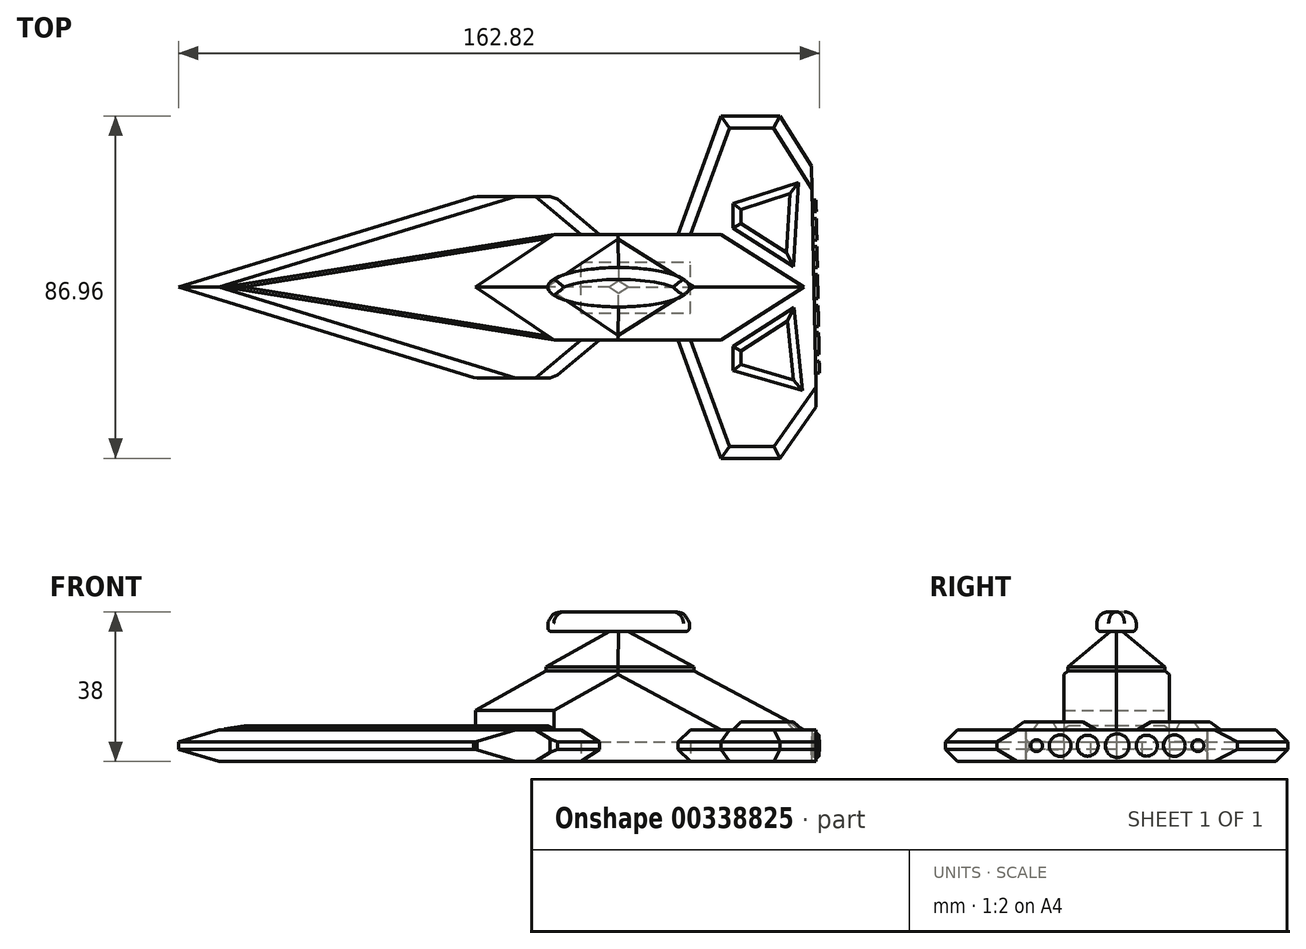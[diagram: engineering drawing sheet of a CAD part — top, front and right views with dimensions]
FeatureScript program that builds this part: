
annotation { "Feature Type Name" : "Feature", "Feature Type Description" : "" }
export const myFeature = defineFeature(function(context is Context, id is Id, definition is map)
    precondition{}
    {
        {
            var Q0;
            Q0=qCreatedBy(makeId("Top.planeOp"),FACE);
            var sketch = newSketch(context, id + "F0", { "sketchPlane" : qUnion([Q0])});
            skLineSegment(sketch, "E0", {"start": v(0, 0) * mm, "end": v(75, 0) * mm});
            skLineSegment(sketch, "E1", {"start": v(0, 0) * mm, "end": v(75.4, 23.05) * mm});
            skLineSegment(sketch, "E2", {"start": v(0, 0) * mm, "end": v(75.4, -23.05) * mm});
            skLineSegment(sketch, "E3", {"start": v(75.4, 23.05) * mm, "end": v(75.4, -23.05) * mm});
            skLineSegment(sketch, "E4", {"start": v(75.4, 23.05) * mm, "end": v(95.4, 23.05) * mm});
            skLineSegment(sketch, "E5", {"start": v(75.4, -23.05) * mm, "end": v(95.4, -23.05) * mm});
            skLineSegment(sketch, "E6", {"start": v(95.4, -23.05) * mm, "end": v(95.4, 23.05) * mm});
            skLineSegment(sketch, "E7", {"start": v(95.4, 23.05) * mm, "end": v(106.9, 13.41) * mm});
            skLineSegment(sketch, "E8", {"start": v(95.4, -23.05) * mm, "end": v(106.9, -13.41) * mm});
            skLineSegment(sketch, "E9", {"start": v(106.9, 13.41) * mm, "end": v(106.9, -13.41) * mm});
            skLineSegment(sketch, "E10", {"start": v(106.9, 13.41) * mm, "end": v(126.9, 13.41) * mm});
            skLineSegment(sketch, "E11", {"start": v(106.9, -13.41) * mm, "end": v(126.9, -13.41) * mm});
            skLineSegment(sketch, "E12", {"start": v(126.9, 13.41) * mm, "end": v(126.9, -13.41) * mm});
            skLineSegment(sketch, "E13", {"start": v(126.9, 13.41) * mm, "end": v(137.84, 43.48) * mm});
            skLineSegment(sketch, "E14", {"start": v(126.9, -13.41) * mm, "end": v(137.84, -43.48) * mm});
            skLineSegment(sketch, "E15", {"start": v(137.84, 43.48) * mm, "end": v(152.84, 43.48) * mm});
            skLineSegment(sketch, "E16", {"start": v(137.84, -43.48) * mm, "end": v(152.84, -43.48) * mm});
            skLineSegment(sketch, "E17", {"start": v(152.84, 43.48) * mm, "end": v(152.84, -43.48) * mm});
            skLineSegment(sketch, "E18", {"start": v(152.84, 43.48) * mm, "end": v(160.79, 30.76) * mm});
            skLineSegment(sketch, "E19", {"start": v(152.84, -43.48) * mm, "end": v(161.98, -30.42) * mm});
            skLineSegment(sketch, "E20", {"start": v(160.79, 30.76) * mm, "end": v(161.98, -30.42) * mm});
            skSolve(sketch);
        }
        {
            var Q0;
            Q0 = qSketchRegion(id + "F0", true);
            extrude(context, id + "F1", {"entities" : qUnion([Q0]), "depth" : 8 * mm});
        }
        {
            var Q0;
            Q0=makeQuery(id+"F1.opExtrude","SWEPT_FACE",FACE,{"disambiguationData":[OSD([sQuery(id+"F0.wireOp",EDGE,"E20")])]});
            var sketch = newSketch(context, id + "F2", { "sketchPlane" : qUnion([Q0])});
            skCircle(sketch, "E21", {"center": v(-2.98, 4) * mm, "radius": 3 * mm});
            skPoint(sketch, "E21.centerSnap0", {"position": v(-33.58, 4) * mm});
            skPoint(sketch, "E21.centerSnap1", {"position": v(-2.98, 0) * mm});
            skCircle(sketch, "E22", {"center": v(-10.48, 4) * mm, "radius": 2.66 * mm});
            skCircle(sketch, "E23", {"center": v(4.52, 4) * mm, "radius": 2.66 * mm});
            skCircle(sketch, "E24", {"center": v(-23.48, 4) * mm, "radius": 1.5 * mm});
            skCircle(sketch, "E25", {"center": v(17.52, 4) * mm, "radius": 1.5 * mm});
            skCircle(sketch, "E26", {"center": v(11.52, 4) * mm, "radius": 2.75 * mm});
            skCircle(sketch, "E27", {"center": v(-17.48, 4) * mm, "radius": 2.75 * mm});
            skSolve(sketch);
        }
        {
            var Q0;
            Q0 = qSketchRegion(id + "F2", true);
            extrude(context, id + "F3", {"entities" : qUnion([Q0]), "operationType" : NewBodyOperationType.ADD, "depth" : 1 * mm});
        }
        {
            var Q0;
            Q0=makeQuery(id+"F1.opExtrude","CAP_FACE",FACE,{"disambiguationData":[OSD([sQuery(id+"F0.wireOp",EDGE,"E1"),sQuery(id+"F0.wireOp",EDGE,"E2"),sQuery(id+"F0.wireOp",EDGE,"E4"),sQuery(id+"F0.wireOp",EDGE,"E5"),sQuery(id+"F0.wireOp",EDGE,"E7"),sQuery(id+"F0.wireOp",EDGE,"E8"),sQuery(id+"F0.wireOp",EDGE,"E10"),sQuery(id+"F0.wireOp",EDGE,"E11"),sQuery(id+"F0.wireOp",EDGE,"E13"),sQuery(id+"F0.wireOp",EDGE,"E14"),sQuery(id+"F0.wireOp",EDGE,"E15"),sQuery(id+"F0.wireOp",EDGE,"E16"),sQuery(id+"F0.wireOp",EDGE,"E18"),sQuery(id+"F0.wireOp",EDGE,"E19"),sQuery(id+"F0.wireOp",EDGE,"E20")])],"isStart":false});
            var sketch = newSketch(context, id + "F4", { "sketchPlane" : qUnion([Q0])});
            skLineSegment(sketch, "E28", {"start": v(95.4, 13.41) * mm, "end": v(75.4, 0) * mm});
            skLineSegment(sketch, "E29", {"start": v(75.4, 0) * mm, "end": v(95.4, -13.41) * mm});
            skLineSegment(sketch, "E30", {"start": v(95.4, -13.41) * mm, "end": v(137.84, -13.41) * mm});
            skLineSegment(sketch, "E31", {"start": v(137.84, -13.41) * mm, "end": v(137.84, 13.41) * mm});
            skLineSegment(sketch, "E32", {"start": v(137.84, 13.41) * mm, "end": v(95.4, 13.41) * mm});
            skLineSegment(sketch, "E33", {"start": v(137.84, 13.41) * mm, "end": v(158.9, 0) * mm});
            skLineSegment(sketch, "E34", {"start": v(158.9, 0) * mm, "end": v(137.84, -13.41) * mm});
            skSolve(sketch);
        }
        {
            var Q0;
            Q0=makeQuery(id+"F4.imprint","IMPRINT",FACE,{"disambiguationData":[TD([[makeQuery(id+"F4.imprint","IMPRINT",EDGE,{"derivedFrom":sQuery(id+"F4.wireOp",EDGE,"E31")}),-1.0]])]});
            var Q1;
            {var subQ4=sQuery(id+"F4.wireOp",EDGE,"E28");Q1=makeQuery(id+"F4.imprint","IMPRINT",FACE,{"disambiguationData":[TD([[makeQuery(id+"F4.imprint","IMPRINT",EDGE,{"derivedFrom":subQ4}),1.0]])]});}
            extrude(context, id + "F5", {"entities" : qUnion([Q0, Q1]), "operationType" : NewBodyOperationType.ADD, "depth" : 15 * mm});
        }
        {
            var Q0;
            Q0=makeQuery(id+"F5.opExtrude","CAP_EDGE",EDGE,{"disambiguationData":[OSD([sQuery(id+"F4.wireOp",EDGE,"E29")])],"isStart":false});
            var Q1;
            Q1=makeQuery(id+"F5.opExtrude","CAP_EDGE",EDGE,{"disambiguationData":[OSD([sQuery(id+"F4.wireOp",EDGE,"E28")])],"isStart":false});
            chamfer(context, id + "F6", {"entities" : qUnion([Q0, Q1]), "width" : 10 * mm, "tangentPropagation" : true});
        }
        {
            var Q0;
            Q0=makeQuery(id+"F5.opExtrude","CAP_EDGE",EDGE,{"disambiguationData":[OSD([sQuery(id+"F4.wireOp",EDGE,"E33")])],"isStart":false});
            var Q1;
            Q1=makeQuery(id+"F5.opExtrude","CAP_EDGE",EDGE,{"disambiguationData":[OSD([sQuery(id+"F4.wireOp",EDGE,"E34")])],"isStart":false});
            chamfer(context, id + "F7", {"entities" : qUnion([Q0, Q1]), "width" : 15 * mm, "tangentPropagation" : true});
        }
        {
            var Q0;
            Q0=makeQuery(id+"F5.opExtrude","CAP_FACE",FACE,{"disambiguationData":[OSD([sQuery(id+"F4.wireOp",EDGE,"E28"),sQuery(id+"F4.wireOp",EDGE,"E29"),sQuery(id+"F4.wireOp",EDGE,"E30"),sQuery(id+"F4.wireOp",EDGE,"E32"),sQuery(id+"F4.wireOp",EDGE,"E33"),sQuery(id+"F4.wireOp",EDGE,"E34")])],"isStart":false});
            var sketch = newSketch(context, id + "F8", { "sketchPlane" : qUnion([Q0])});
            skLineSegment(sketch, "E35", {"start": v(111.68, 12.28) * mm, "end": v(111.68, 0) * mm});
            skLineSegment(sketch, "E36", {"start": v(111.68, 0) * mm, "end": v(111.68, -12.28) * mm});
            skLineSegment(sketch, "E37", {"start": v(111.68, -12.28) * mm, "end": v(130.98, 0) * mm});
            skLineSegment(sketch, "E38", {"start": v(130.98, 0) * mm, "end": v(111.68, 0) * mm});
            skLineSegment(sketch, "E39", {"start": v(93.36, 0) * mm, "end": v(111.68, 0) * mm});
            skLineSegment(sketch, "E40", {"start": v(111.68, 12.28) * mm, "end": v(93.36, 0) * mm});
            skLineSegment(sketch, "E41", {"start": v(130.98, 0) * mm, "end": v(111.68, 12.28) * mm});
            skSolve(sketch);
        }
        {
            var Q0;
            Q0=makeQuery(id+"F8.imprint","IMPRINT",FACE,{"disambiguationData":[TD([[makeQuery(id+"F8.imprint","IMPRINT",EDGE,{"derivedFrom":sQuery(id+"F8.wireOp",EDGE,"E36")}),-1.0]])]});
            var Q1;
            Q1=makeQuery(id+"F8.imprint","IMPRINT",FACE,{"disambiguationData":[TD([[makeQuery(id+"F8.imprint","IMPRINT",EDGE,{"derivedFrom":sQuery(id+"F8.wireOp",EDGE,"E36")}),1.0]])]});
            var Q2;
            Q2=makeQuery(id+"F8.imprint","IMPRINT",FACE,{"disambiguationData":[TD([[makeQuery(id+"F8.imprint","IMPRINT",EDGE,{"derivedFrom":sQuery(id+"F8.wireOp",EDGE,"E35")}),-1.0]])]});
            var Q3;
            Q3=makeQuery(id+"F8.imprint","IMPRINT",FACE,{"disambiguationData":[TD([[makeQuery(id+"F8.imprint","IMPRINT",EDGE,{"derivedFrom":sQuery(id+"F8.wireOp",EDGE,"E35")}),1.0]])]});
            extrude(context, id + "F9", {"entities" : qUnion([Q0, Q1, Q2, Q3]), "operationType" : NewBodyOperationType.ADD, "depth" : 10 * mm});
        }
        {
            var Q0;
            Q0=makeQuery(id+"F9.opExtrude","CAP_EDGE",EDGE,{"disambiguationData":[OSD([sQuery(id+"F8.wireOp",EDGE,"E37")])],"isStart":false});
            var Q1;
            Q1=makeQuery(id+"F9.opExtrude","CAP_EDGE",EDGE,{"disambiguationData":[OSD([sQuery(id+"F4.wireOp",EDGE,"E28"),sQuery(id+"F4.wireOp",EDGE,"E29"),sQuery(id+"F4.wireOp",EDGE,"E30"),sQuery(id+"F4.wireOp",EDGE,"E32"),sQuery(id+"F4.wireOp",EDGE,"E33"),sQuery(id+"F4.wireOp",EDGE,"E34")])],"isStart":false});
            var Q2;
            Q2=makeQuery(id+"F9.opExtrude","CAP_EDGE",EDGE,{"disambiguationData":[OSD([sQuery(id+"F8.wireOp",EDGE,"E40")])],"isStart":false});
            var Q3;
            Q3=makeQuery(id+"F9.opExtrude","CAP_EDGE",EDGE,{"disambiguationData":[OSD([sQuery(id+"F8.wireOp",EDGE,"E41")])],"isStart":false});
            chamfer(context, id + "F10", {"entities" : qUnion([Q0, Q1, Q2, Q3]), "width" : 9 * mm, "tangentPropagation" : true});
        }
        {
            var Q0;
            Q0=makeQuery(id+"F9.opExtrude","CAP_FACE",FACE,{"disambiguationData":[OSD([sQuery(id+"F4.wireOp",EDGE,"E28"),sQuery(id+"F4.wireOp",EDGE,"E29"),sQuery(id+"F4.wireOp",EDGE,"E30"),sQuery(id+"F4.wireOp",EDGE,"E32"),sQuery(id+"F4.wireOp",EDGE,"E33"),sQuery(id+"F4.wireOp",EDGE,"E34"),sQuery(id+"F8.wireOp",EDGE,"E37"),sQuery(id+"F8.wireOp",EDGE,"E40"),sQuery(id+"F8.wireOp",EDGE,"E41")])],"isStart":false});
            var sketch = newSketch(context, id + "F11", { "sketchPlane" : qUnion([Q0])});
            skEllipse(sketch, "E42", {"center": v(111.8, 0) * mm, "majorRadius": 18 * mm, "minorRadius": 5 * mm, "majorAxis": v(-1, 0)});
            skSolve(sketch);
        }
        {
            var Q0;
            Q0 = qSketchRegion(id + "F11", true);
            extrude(context, id + "F12", {"entities" : qUnion([Q0]), "operationType" : NewBodyOperationType.ADD, "depth" : 5 * mm});
        }
        {
            var Q0;
            Q0=makeQuery(id+"F12.opExtrude","CAP_EDGE",EDGE,{"disambiguationData":[OSD([sQuery(id+"F11.wireOp",EDGE,"E42")])],"isStart":false});
            fillet(context, id + "F13", {"entities" : qUnion([Q0]), "radius" : 3 * mm, "tangentPropagation" : true, "allowEdgeOverflow" : false});
        }
        {
            var Q0;
            Q0=makeQuery(id+"F12.opExtrude","CAP_EDGE",EDGE,{"disambiguationData":[OSD([sQuery(id+"F11.wireOp",EDGE,"E42")])],"isStart":true});
            fillet(context, id + "F14", {"entities" : qUnion([Q0]), "radius" : 1 * mm, "tangentPropagation" : true, "allowEdgeOverflow" : false});
        }
        {
            var Q0;
            {var subQ0=sQuery(id+"F0.wireOp",EDGE,"E11");var subQ1=sQuery(id+"F0.wireOp",EDGE,"E10");var subQ2=sQuery(id+"F0.wireOp",EDGE,"E8");var subQ3=sQuery(id+"F0.wireOp",EDGE,"E7");var subQ4=sQuery(id+"F0.wireOp",EDGE,"E1");var subQ5=sQuery(id+"F0.wireOp",EDGE,"E5");var subQ6=sQuery(id+"F0.wireOp",EDGE,"E2");var subQ7=sQuery(id+"F0.wireOp",EDGE,"E4");Q0=makeQuery(id+"F5.boolean.opBoolean","SPLIT",FACE,{"disambiguationData":[TD([makeQuery(id+"F1.opExtrude","SWEPT_FACE",FACE,{"disambiguationData":[OSD([subQ4])]})])],"derivedFrom":makeQuery(id+"F1.opExtrude","CAP_FACE",FACE,{"disambiguationData":[OSD([subQ4,subQ6,subQ7,subQ5,subQ3,subQ2,subQ1,subQ0,sQuery(id+"F0.wireOp",EDGE,"E13"),sQuery(id+"F0.wireOp",EDGE,"E14"),sQuery(id+"F0.wireOp",EDGE,"E15"),sQuery(id+"F0.wireOp",EDGE,"E16"),sQuery(id+"F0.wireOp",EDGE,"E18"),sQuery(id+"F0.wireOp",EDGE,"E19"),sQuery(id+"F0.wireOp",EDGE,"E20")])],"isStart":false})});}
            var sketch = newSketch(context, id + "F15", { "sketchPlane" : qUnion([Q0])});
            skLineSegment(sketch, "E43", {"start": v(11.59, 0) * mm, "end": v(95.4, 13.41) * mm});
            skLineSegment(sketch, "E44", {"start": v(95.4, 13.41) * mm, "end": v(75.4, 0) * mm});
            skLineSegment(sketch, "E45", {"start": v(75.4, 0) * mm, "end": v(95.4, -13.41) * mm});
            skLineSegment(sketch, "E46", {"start": v(95.4, -13.41) * mm, "end": v(11.59, 0) * mm});
            skLineSegment(sketch, "E47", {"start": v(75.4, 0) * mm, "end": v(11.59, 0) * mm});
            skSolve(sketch);
        }
        {
            var Q0;
            Q0=makeQuery(id+"F15.imprint","IMPRINT",FACE,{"disambiguationData":[TD([[makeQuery(id+"F15.imprint","IMPRINT",EDGE,{"derivedFrom":sQuery(id+"F15.wireOp",EDGE,"E43")}),-1.0]])]});
            var Q1;
            Q1=makeQuery(id+"F15.imprint","IMPRINT",FACE,{"disambiguationData":[TD([[makeQuery(id+"F15.imprint","IMPRINT",EDGE,{"derivedFrom":sQuery(id+"F15.wireOp",EDGE,"E45")}),-1.0]])]});
            extrude(context, id + "F16", {"entities" : qUnion([Q0, Q1]), "operationType" : NewBodyOperationType.ADD, "depth" : 1 * mm});
        }
        {
            var Q0;
            Q0=makeQuery(id+"F16.opExtrude","CAP_EDGE",EDGE,{"disambiguationData":[OSD([sQuery(id+"F15.wireOp",EDGE,"E46")])],"isStart":false});
            var Q1;
            Q1=makeQuery(id+"F16.opExtrude","CAP_EDGE",EDGE,{"disambiguationData":[OSD([sQuery(id+"F15.wireOp",EDGE,"E43")])],"isStart":false});
            chamfer(context, id + "F17", {"entities" : qUnion([Q0, Q1]), "width" : 0.8 * mm, "tangentPropagation" : true});
        }
        {
            var Q0;
            {var subQ0=sQuery(id+"F0.wireOp",EDGE,"E20");var subQ1=sQuery(id+"F0.wireOp",EDGE,"E19");var subQ2=sQuery(id+"F0.wireOp",EDGE,"E18");var subQ3=sQuery(id+"F0.wireOp",EDGE,"E16");var subQ4=sQuery(id+"F0.wireOp",EDGE,"E15");var subQ5=sQuery(id+"F0.wireOp",EDGE,"E10");var subQ6=sQuery(id+"F0.wireOp",EDGE,"E11");var subQ7=sQuery(id+"F0.wireOp",EDGE,"E13");var subQ8=sQuery(id+"F0.wireOp",EDGE,"E14");Q0=makeQuery(id+"F5.boolean.opBoolean","SPLIT",FACE,{"disambiguationData":[TD([makeQuery(id+"F1.opExtrude","SWEPT_FACE",FACE,{"disambiguationData":[OSD([subQ7])]})])],"derivedFrom":makeQuery(id+"F1.opExtrude","CAP_FACE",FACE,{"disambiguationData":[OSD([sQuery(id+"F0.wireOp",EDGE,"E1"),sQuery(id+"F0.wireOp",EDGE,"E2"),sQuery(id+"F0.wireOp",EDGE,"E4"),sQuery(id+"F0.wireOp",EDGE,"E5"),sQuery(id+"F0.wireOp",EDGE,"E7"),sQuery(id+"F0.wireOp",EDGE,"E8"),subQ5,subQ6,subQ7,subQ8,subQ4,subQ3,subQ2,subQ1,subQ0])],"isStart":false})});}
            var sketch = newSketch(context, id + "F18", { "sketchPlane" : qUnion([Q0])});
            skLineSegment(sketch, "E48", {"start": v(137.84, 13.41) * mm, "end": v(137.84, 23.41) * mm});
            skLineSegment(sketch, "E49", {"start": v(137.84, 23.41) * mm, "end": v(160.79, 30.76) * mm});
            skLineSegment(sketch, "E50", {"start": v(160.79, 30.76) * mm, "end": v(158.9, 0) * mm});
            skLineSegment(sketch, "E51", {"start": v(137.84, -13.41) * mm, "end": v(137.84, -23.41) * mm});
            skLineSegment(sketch, "E52", {"start": v(137.84, -23.41) * mm, "end": v(161.98, -30.42) * mm});
            skLineSegment(sketch, "E53", {"start": v(161.98, -30.42) * mm, "end": v(158.9, 0) * mm});
            skSolve(sketch);
        }
        {
            var Q0;
            Q0=makeQuery(id+"F18.imprint","IMPRINT",FACE,{"disambiguationData":[TD([[makeQuery(id+"F18.imprint","IMPRINT",EDGE,{"derivedFrom":sQuery(id+"F18.wireOp",EDGE,"E48")}),-1.0]])]});
            var Q1;
            Q1=makeQuery(id+"F18.imprint","IMPRINT",FACE,{"disambiguationData":[TD([[makeQuery(id+"F18.imprint","IMPRINT",EDGE,{"derivedFrom":sQuery(id+"F18.wireOp",EDGE,"E51")}),1.0]])]});
            extrude(context, id + "F19", {"entities" : qUnion([Q0, Q1]), "depth" : 2 * mm});
        }
        {
            var Q0;
            Q0=makeQuery(id+"F19.opExtrude","CAP_EDGE",EDGE,{"disambiguationData":[OSD([sQuery(id+"F18.wireOp",EDGE,"E51")])],"isStart":false});
            var Q1;
            Q1=makeQuery(id+"F19.opExtrude","CAP_EDGE",EDGE,{"disambiguationData":[OSD([sQuery(id+"F18.wireOp",EDGE,"E52")])],"isStart":false});
            var Q2;
            Q2=makeQuery(id+"F19.opExtrude","CAP_EDGE",EDGE,{"disambiguationData":[OSD([sQuery(id+"F18.wireOp",EDGE,"E48")])],"isStart":false});
            var Q3;
            Q3=makeQuery(id+"F19.opExtrude","CAP_EDGE",EDGE,{"disambiguationData":[OSD([sQuery(id+"F18.wireOp",EDGE,"E49")])],"isStart":false});
            var Q4;
            Q4=makeQuery(id+"F19.opExtrude","CAP_EDGE",EDGE,{"disambiguationData":[OSD([sQuery(id+"F18.wireOp",EDGE,"E50")])],"isStart":false});
            var Q5;
            Q5=makeQuery(id+"F19.opExtrude","CAP_EDGE",EDGE,{"disambiguationData":[OSD([sQuery(id+"F18.wireOp",EDGE,"E53")])],"isStart":false});
            var Q6;
            Q6=makeQuery(id+"F19.opExtrude","CAP_EDGE",EDGE,{"disambiguationData":[OSD([sQuery(id+"F0.wireOp",EDGE,"E1"),sQuery(id+"F0.wireOp",EDGE,"E2"),sQuery(id+"F0.wireOp",EDGE,"E4"),sQuery(id+"F0.wireOp",EDGE,"E5"),sQuery(id+"F0.wireOp",EDGE,"E7"),sQuery(id+"F0.wireOp",EDGE,"E8"),sQuery(id+"F0.wireOp",EDGE,"E10"),sQuery(id+"F0.wireOp",EDGE,"E11"),sQuery(id+"F0.wireOp",EDGE,"E13"),sQuery(id+"F0.wireOp",EDGE,"E14"),sQuery(id+"F0.wireOp",EDGE,"E15"),sQuery(id+"F0.wireOp",EDGE,"E16"),sQuery(id+"F0.wireOp",EDGE,"E18"),sQuery(id+"F0.wireOp",EDGE,"E19"),sQuery(id+"F0.wireOp",EDGE,"E20"),sQuery(id+"F4.wireOp",EDGE,"E34")])],"isStart":false});
            var Q7;
            Q7=makeQuery(id+"F19.opExtrude","CAP_EDGE",EDGE,{"disambiguationData":[OSD([sQuery(id+"F0.wireOp",EDGE,"E1"),sQuery(id+"F0.wireOp",EDGE,"E2"),sQuery(id+"F0.wireOp",EDGE,"E4"),sQuery(id+"F0.wireOp",EDGE,"E5"),sQuery(id+"F0.wireOp",EDGE,"E7"),sQuery(id+"F0.wireOp",EDGE,"E8"),sQuery(id+"F0.wireOp",EDGE,"E10"),sQuery(id+"F0.wireOp",EDGE,"E11"),sQuery(id+"F0.wireOp",EDGE,"E13"),sQuery(id+"F0.wireOp",EDGE,"E14"),sQuery(id+"F0.wireOp",EDGE,"E15"),sQuery(id+"F0.wireOp",EDGE,"E16"),sQuery(id+"F0.wireOp",EDGE,"E18"),sQuery(id+"F0.wireOp",EDGE,"E19"),sQuery(id+"F0.wireOp",EDGE,"E20"),sQuery(id+"F4.wireOp",EDGE,"E33")])],"isStart":false});
            chamfer(context, id + "F20", {"entities" : qUnion([Q0, Q1, Q2, Q3, Q4, Q5, Q6, Q7]), "width" : 5 * mm, "tangentPropagation" : true});
        }
        {
            var Q0;
            Q0=makeQuery(id+"F1.opExtrude","CAP_EDGE",EDGE,{"disambiguationData":[OSD([sQuery(id+"F0.wireOp",EDGE,"E2")])],"isStart":false});
            var Q1;
            Q1=makeQuery(id+"F1.opExtrude","CAP_EDGE",EDGE,{"disambiguationData":[OSD([sQuery(id+"F0.wireOp",EDGE,"E1")])],"isStart":false});
            var Q2;
            Q2=makeQuery(id+"F1.opExtrude","CAP_EDGE",EDGE,{"disambiguationData":[OSD([sQuery(id+"F0.wireOp",EDGE,"E2")])],"isStart":true});
            var Q3;
            Q3=makeQuery(id+"F1.opExtrude","CAP_EDGE",EDGE,{"disambiguationData":[OSD([sQuery(id+"F0.wireOp",EDGE,"E1")])],"isStart":true});
            var Q4;
            Q4=makeQuery(id+"F1.opExtrude","CAP_EDGE",EDGE,{"disambiguationData":[OSD([sQuery(id+"F0.wireOp",EDGE,"E8")])],"isStart":false});
            var Q5;
            Q5=makeQuery(id+"F1.opExtrude","CAP_EDGE",EDGE,{"disambiguationData":[OSD([sQuery(id+"F0.wireOp",EDGE,"E8")])],"isStart":true});
            var Q6;
            Q6=makeQuery(id+"F1.opExtrude","SWEPT_EDGE",EDGE,{"disambiguationData":[OSD([sQuery(id+"F0.wireOp",EDGE,"E5"),sQuery(id+"F0.wireOp",EDGE,"E6"),sQuery(id+"F0.wireOp",EDGE,"E8")])]});
            var Q7;
            Q7=makeQuery(id+"F1.opExtrude","CAP_EDGE",EDGE,{"disambiguationData":[OSD([sQuery(id+"F0.wireOp",EDGE,"E14")])],"isStart":false});
            var Q8;
            Q8=makeQuery(id+"F1.opExtrude","CAP_EDGE",EDGE,{"disambiguationData":[OSD([sQuery(id+"F0.wireOp",EDGE,"E14")])],"isStart":true});
            var Q9;
            Q9=makeQuery(id+"F1.opExtrude","CAP_EDGE",EDGE,{"disambiguationData":[OSD([sQuery(id+"F0.wireOp",EDGE,"E13")])],"isStart":false});
            var Q10;
            Q10=makeQuery(id+"F1.opExtrude","CAP_EDGE",EDGE,{"disambiguationData":[OSD([sQuery(id+"F0.wireOp",EDGE,"E13")])],"isStart":true});
            var Q11;
            Q11=makeQuery(id+"F1.opExtrude","CAP_EDGE",EDGE,{"disambiguationData":[OSD([sQuery(id+"F0.wireOp",EDGE,"E15")])],"isStart":false});
            var Q12;
            Q12=makeQuery(id+"F1.opExtrude","CAP_EDGE",EDGE,{"disambiguationData":[OSD([sQuery(id+"F0.wireOp",EDGE,"E15")])],"isStart":true});
            var Q13;
            Q13=makeQuery(id+"F1.opExtrude","CAP_EDGE",EDGE,{"disambiguationData":[OSD([sQuery(id+"F0.wireOp",EDGE,"E18")])],"isStart":false});
            var Q14;
            Q14=makeQuery(id+"F1.opExtrude","CAP_EDGE",EDGE,{"disambiguationData":[OSD([sQuery(id+"F0.wireOp",EDGE,"E18")])],"isStart":true});
            var Q15;
            Q15=makeQuery(id+"F1.opExtrude","CAP_EDGE",EDGE,{"disambiguationData":[OSD([sQuery(id+"F0.wireOp",EDGE,"E19")])],"isStart":false});
            var Q16;
            Q16=makeQuery(id+"F1.opExtrude","CAP_EDGE",EDGE,{"disambiguationData":[OSD([sQuery(id+"F0.wireOp",EDGE,"E19")])],"isStart":true});
            var Q17;
            Q17=makeQuery(id+"F1.opExtrude","CAP_EDGE",EDGE,{"disambiguationData":[OSD([sQuery(id+"F0.wireOp",EDGE,"E16")])],"isStart":true});
            var Q18;
            Q18=makeQuery(id+"F1.opExtrude","CAP_EDGE",EDGE,{"disambiguationData":[OSD([sQuery(id+"F0.wireOp",EDGE,"E16")])],"isStart":false});
            var Q19;
            Q19=makeQuery(id+"F1.opExtrude","CAP_EDGE",EDGE,{"disambiguationData":[OSD([sQuery(id+"F0.wireOp",EDGE,"E7")])],"isStart":false});
            var Q20;
            Q20=makeQuery(id+"F1.opExtrude","CAP_EDGE",EDGE,{"disambiguationData":[OSD([sQuery(id+"F0.wireOp",EDGE,"E7")])],"isStart":true});
            var Q21;
            Q21=makeQuery(id+"F1.opExtrude","SWEPT_EDGE",EDGE,{"disambiguationData":[OSD([sQuery(id+"F0.wireOp",EDGE,"E4"),sQuery(id+"F0.wireOp",EDGE,"E6"),sQuery(id+"F0.wireOp",EDGE,"E7")])]});
            var Q22;
            Q22=makeQuery(id+"F1.opExtrude","SWEPT_EDGE",EDGE,{"disambiguationData":[OSD([sQuery(id+"F0.wireOp",EDGE,"E1"),sQuery(id+"F0.wireOp",EDGE,"E3"),sQuery(id+"F0.wireOp",EDGE,"E4")])]});
            var Q23;
            Q23=makeQuery(id+"F1.opExtrude","SWEPT_EDGE",EDGE,{"disambiguationData":[OSD([sQuery(id+"F0.wireOp",EDGE,"E2"),sQuery(id+"F0.wireOp",EDGE,"E3"),sQuery(id+"F0.wireOp",EDGE,"E5")])]});
            chamfer(context, id + "F21", {"entities" : qUnion([Q0, Q1, Q2, Q3, Q4, Q5, Q6, Q7, Q8, Q9, Q10, Q11, Q12, Q13, Q14, Q15, Q16, Q17, Q18, Q19, Q20, Q21, Q22, Q23]), "width" : 3 * mm, "tangentPropagation" : true});
        }
        {
            var Q0;
            Q0=makeQuery(id+"F1.opExtrude","CAP_FACE",FACE,{"disambiguationData":[OSD([sQuery(id+"F0.wireOp",EDGE,"E1"),sQuery(id+"F0.wireOp",EDGE,"E2"),sQuery(id+"F0.wireOp",EDGE,"E4"),sQuery(id+"F0.wireOp",EDGE,"E5"),sQuery(id+"F0.wireOp",EDGE,"E7"),sQuery(id+"F0.wireOp",EDGE,"E8"),sQuery(id+"F0.wireOp",EDGE,"E10"),sQuery(id+"F0.wireOp",EDGE,"E11"),sQuery(id+"F0.wireOp",EDGE,"E13"),sQuery(id+"F0.wireOp",EDGE,"E14"),sQuery(id+"F0.wireOp",EDGE,"E15"),sQuery(id+"F0.wireOp",EDGE,"E16"),sQuery(id+"F0.wireOp",EDGE,"E18"),sQuery(id+"F0.wireOp",EDGE,"E19"),sQuery(id+"F0.wireOp",EDGE,"E20")])],"isStart":true});
            var sketch = newSketch(context, id + "F22", { "sketchPlane" : qUnion([Q0])});
            skLineSegment(sketch, "E54.bottom", {"start": v(102.23, 6.59) * mm, "end": v(130.09, 6.59) * mm});
            skLineSegment(sketch, "E54.top", {"start": v(102.23, -6.41) * mm, "end": v(130.09, -6.41) * mm});
            skLineSegment(sketch, "E54.left", {"start": v(102.23, 6.59) * mm, "end": v(102.23, -6.41) * mm});
            skLineSegment(sketch, "E54.right", {"start": v(130.09, 6.59) * mm, "end": v(130.09, -6.41) * mm});
            skSolve(sketch);
        }
        {
            var Q0;
            Q0 = qSketchRegion(id + "F22", true);
            extrude(context, id + "F23", {"entities" : qUnion([Q0]), "operationType" : NewBodyOperationType.REMOVE, "oppositeDirection" : true, "depth" : 5 * mm});
        }
    });
